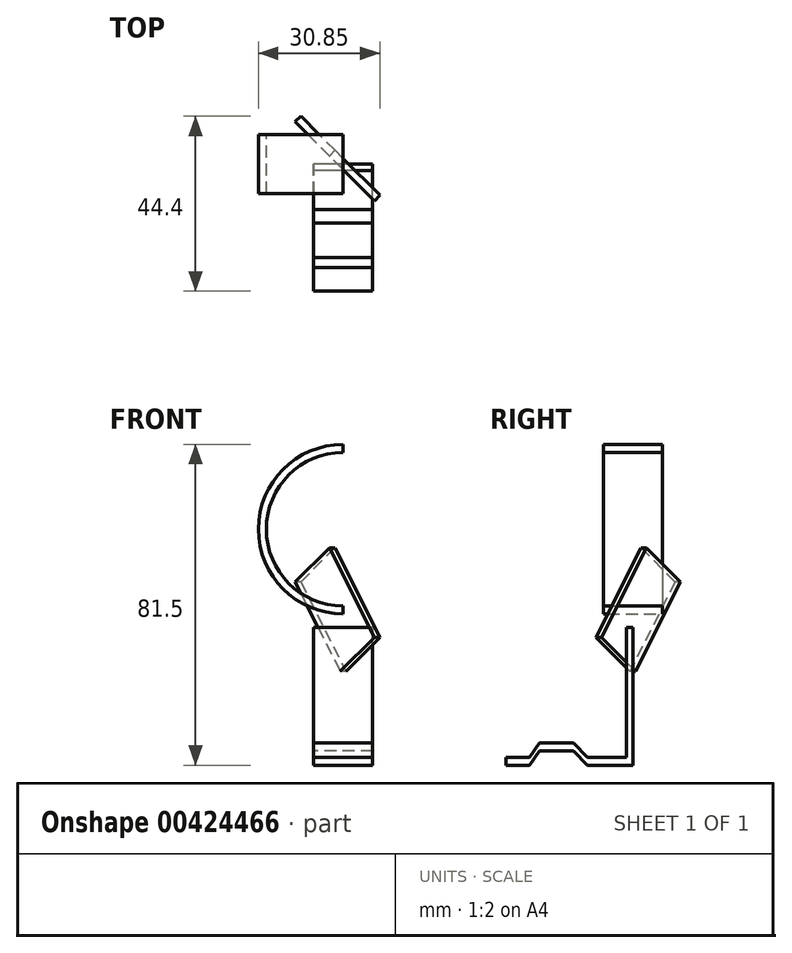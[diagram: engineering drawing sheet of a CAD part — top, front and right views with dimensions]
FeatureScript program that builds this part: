
annotation { "Feature Type Name" : "Feature", "Feature Type Description" : "" }
export const myFeature = defineFeature(function(context is Context, id is Id, definition is map)
    precondition{}
    {
        {
            var Q0;
            Q0=qCreatedBy(makeId("Front.planeOp"),FACE);
            var sketch = newSketch(context, id + "F0", { "sketchPlane" : qUnion([Q0])});
            skLineSegment(sketch, "E0", {"start": v(0, 0) * mm, "end": v(0, 97.76) * mm, "construction": true});
            skArc(sketch, "E1", {"start": v(0, 79.5) * mm, "mid": v(-19.5, 60) * mm, "end": v(0, 40.5) * mm});
            skArc(sketch, "E2", {"start": v(0, 81.5) * mm, "mid": v(-21.5, 60) * mm, "end": v(0, 38.5) * mm});
            skLineSegment(sketch, "E3", {"start": v(0, 81.5) * mm, "end": v(0, 79.5) * mm});
            skLineSegment(sketch, "E4", {"start": v(0, 40.5) * mm, "end": v(0, 38.5) * mm});
            skSolve(sketch);
        }
        {
            var Q0;
            Q0 = qSketchRegion(id + "F0", true);
            extrude(context, id + "F1", {"entities" : qUnion([Q0]), "endBound" : BoundingType.SYMMETRIC, "depth" : 15 * mm});
        }
        {
            var Q0;
            Q0=qCreatedBy(makeId("Right.planeOp"),FACE);
            var sketch = newSketch(context, id + "F2", { "sketchPlane" : qUnion([Q0])});
            skLineSegment(sketch, "E5", {"start": v(0, 35.07) * mm, "end": v(0, 0) * mm});
            skLineSegment(sketch, "E6", {"start": v(0, 0) * mm, "end": v(-11.51, 0) * mm});
            skLineSegment(sketch, "E7", {"start": v(-11.51, 0) * mm, "end": v(-15.04, 3.7) * mm});
            skLineSegment(sketch, "E8", {"start": v(-15.04, 3.7) * mm, "end": v(-23.74, 3.7) * mm});
            skLineSegment(sketch, "E9", {"start": v(-23.74, 3.7) * mm, "end": v(-26.28, 0) * mm});
            skLineSegment(sketch, "E10", {"start": v(-26.28, 0) * mm, "end": v(-32.26, 0) * mm});
            skLineSegment(sketch, "E11", {"start": v(-32.26, 0) * mm, "end": v(-32.26, 2) * mm});
            skLineSegment(sketch, "E12", {"start": v(-32.26, 2) * mm, "end": v(-26.28, 2) * mm});
            skLineSegment(sketch, "E13", {"start": v(-26.28, 2) * mm, "end": v(-23.74, 5.7) * mm});
            skLineSegment(sketch, "E14", {"start": v(-23.74, 5.7) * mm, "end": v(-15.04, 5.7) * mm});
            skLineSegment(sketch, "E15", {"start": v(-15.04, 5.7) * mm, "end": v(-11.51, 2) * mm});
            skLineSegment(sketch, "E16", {"start": v(-11.51, 2) * mm, "end": v(-1.62, 2) * mm});
            skLineSegment(sketch, "E17", {"start": v(-1.62, 2) * mm, "end": v(-1.62, 35.07) * mm});
            skLineSegment(sketch, "E18", {"start": v(-1.62, 35.07) * mm, "end": v(0, 35.07) * mm});
            skLineSegment(sketch, "E19", {"start": v(-23.74, 5.7) * mm, "end": v(-23.74, 3.7) * mm, "construction": true});
            skSolve(sketch);
        }
        {
            var Q0;
            Q0 = qSketchRegion(id + "F2", true);
            extrude(context, id + "F3", {"entities" : qUnion([Q0]), "endBound" : BoundingType.SYMMETRIC, "depth" : 15 * mm});
        }
        {
            var Q0;
            Q0=qCreatedBy(makeId("Right.planeOp"),FACE);
            var Q1;
            Q1=qCreatedBy(makeId("Front.planeOp"),FACE);
            cPlane(context, id + "F4", {"entities" : qUnion([Q0, Q1]), "cplaneType" : CPlaneType.MID_PLANE, "offset" : 25 * mm, "width" : 150 * mm, "height" : 150 * mm});
        }
        {
            var Q0;
            Q0=qCreatedBy(id+"F4.planeOp",FACE);
            var sketch = newSketch(context, id + "F5", { "sketchPlane" : qUnion([Q0])});
            skLineSegment(sketch, "E20", {"start": v(16.17, 46.58) * mm, "end": v(0, 23.84) * mm});
            skLineSegment(sketch, "E21", {"start": v(0, 23.84) * mm, "end": v(-12.23, 32.53) * mm});
            skLineSegment(sketch, "E22", {"start": v(-12.23, 32.53) * mm, "end": v(3.94, 55.27) * mm});
            skLineSegment(sketch, "E23", {"start": v(3.94, 55.27) * mm, "end": v(16.17, 46.58) * mm});
            skSolve(sketch);
        }
        {
            var Q0;
            Q0 = qSketchRegion(id + "F5", true);
            extrude(context, id + "F6", {"entities" : qUnion([Q0]), "endBound" : BoundingType.SYMMETRIC, "depth" : 2 * mm});
        }
    });
